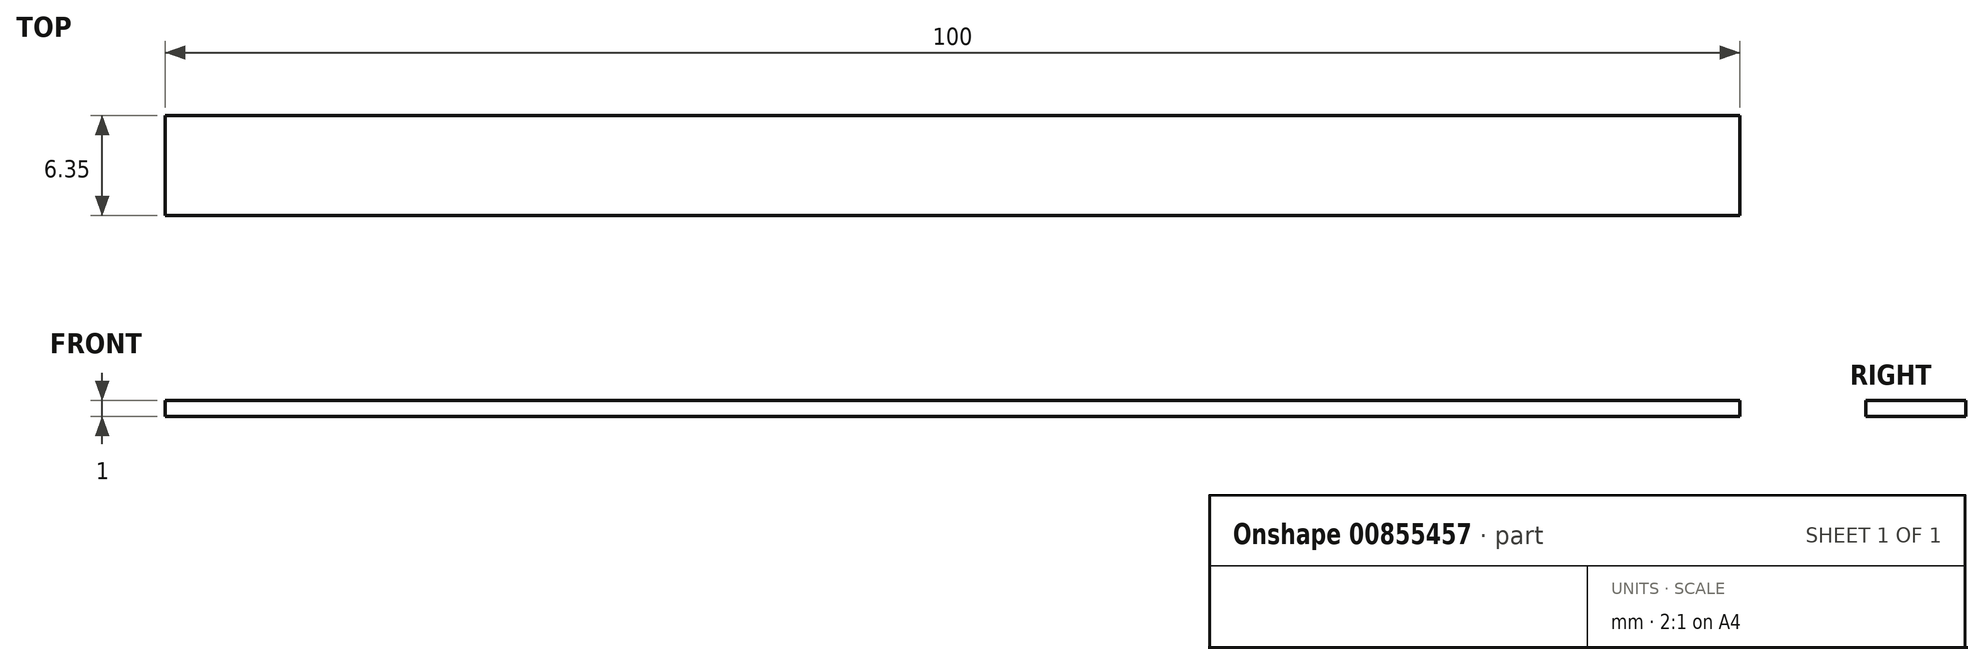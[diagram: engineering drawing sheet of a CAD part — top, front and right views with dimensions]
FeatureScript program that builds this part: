
annotation { "Feature Type Name" : "Feature", "Feature Type Description" : "" }
export const myFeature = defineFeature(function(context is Context, id is Id, definition is map)
    precondition{}
    {
        {
            var Q0;
            Q0=qCreatedBy(makeId("Top.planeOp"),FACE);
            var sketch = newSketch(context, id + "F0", { "sketchPlane" : qUnion([Q0])});
            skLineSegment(sketch, "E0.bottom", {"start": v(0, 0) * mm, "end": v(100, 0) * mm});
            skLineSegment(sketch, "E0.top", {"start": v(0, -6.35) * mm, "end": v(100, -6.35) * mm});
            skLineSegment(sketch, "E0.left", {"start": v(0, 0) * mm, "end": v(0, -6.35) * mm});
            skLineSegment(sketch, "E0.right", {"start": v(100, 0) * mm, "end": v(100, -6.35) * mm});
            skSolve(sketch);
        }
        {
            var Q0;
            Q0=makeQuery(id+"F0.imprint","IMPRINT",FACE,{"disambiguationData":[TD([[makeQuery(id+"F0.imprint","IMPRINT",EDGE,{"derivedFrom":sQuery(id+"F0.wireOp",EDGE,"E0.bottom")}),-1.0]])]});
            extrude(context, id + "F1", {"entities" : qUnion([Q0]), "depth" : 1 * mm, "offsetDistance" : 25 * mm});
        }
    });
